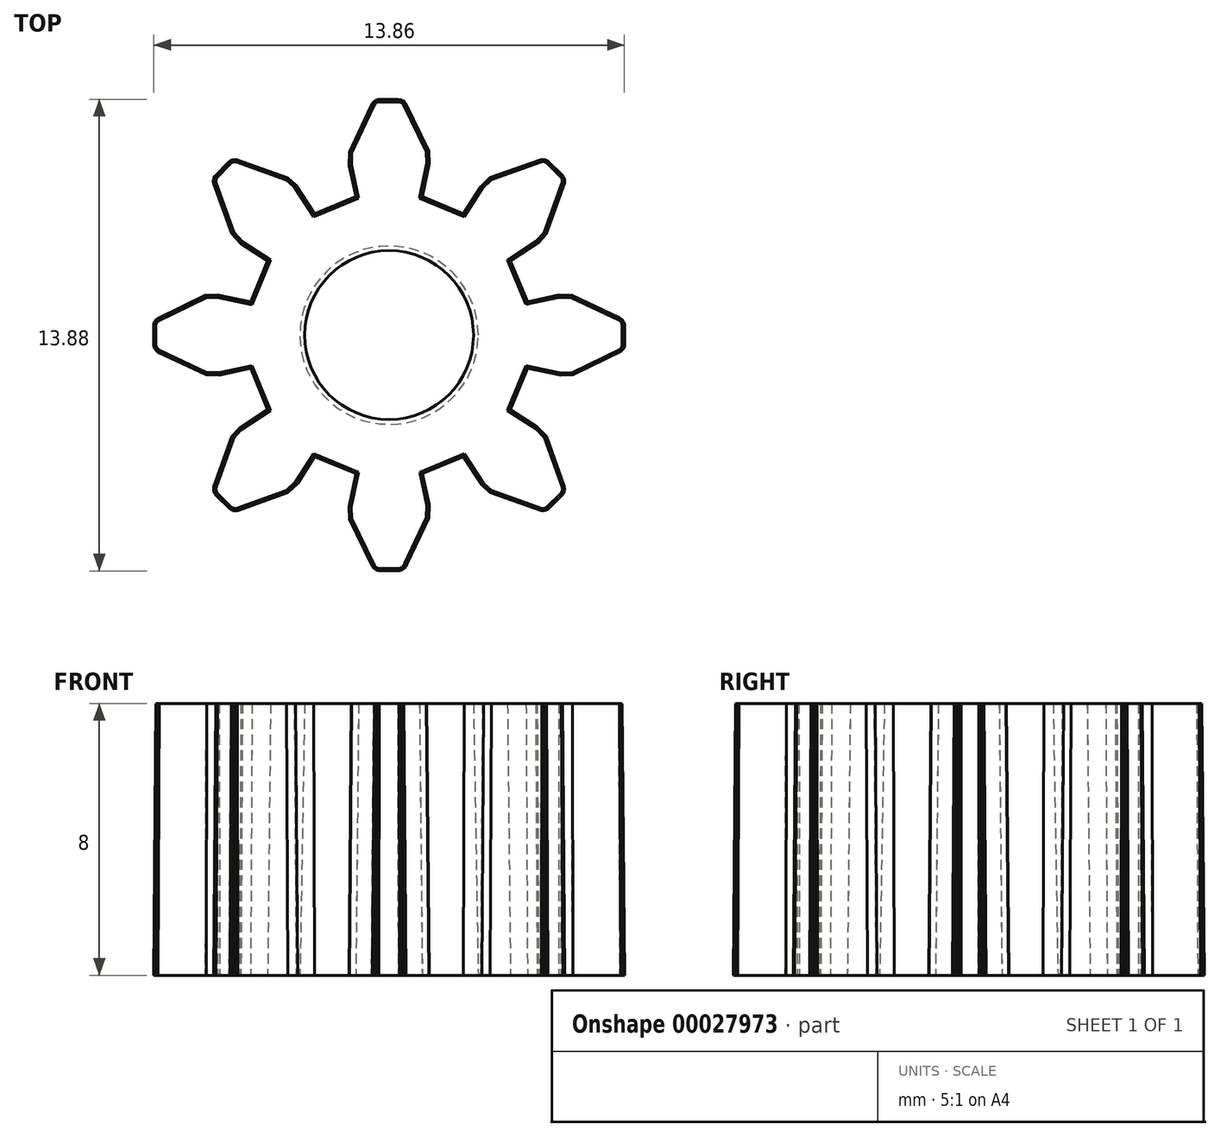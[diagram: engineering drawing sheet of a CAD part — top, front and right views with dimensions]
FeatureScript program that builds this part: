
annotation { "Feature Type Name" : "Feature", "Feature Type Description" : "" }
export const myFeature = defineFeature(function(context is Context, id is Id, definition is map)
    precondition{}
    {
        {
            var Q0;
            Q0=qCreatedBy(makeId("Top.planeOp"),FACE);
            var sketch = newSketch(context, id + "F0", { "sketchPlane" : qUnion([Q0])});
            skLineSegment(sketch, "E0", {"start": v(0.02, 6.93) * mm, "end": v(-0.31, 6.93) * mm});
            skLineSegment(sketch, "E1", {"start": v(-0.31, 6.93) * mm, "end": v(-0.39, 6.9) * mm});
            skLineSegment(sketch, "E2", {"start": v(-0.39, 6.9) * mm, "end": v(-0.43, 6.88) * mm});
            skLineSegment(sketch, "E3", {"start": v(-0.43, 6.88) * mm, "end": v(-0.48, 6.83) * mm});
            skLineSegment(sketch, "E4", {"start": v(-0.48, 6.83) * mm, "end": v(-0.53, 6.74) * mm});
            skLineSegment(sketch, "E5", {"start": v(-0.53, 6.74) * mm, "end": v(-1.17, 5.38) * mm});
            skLineSegment(sketch, "E6", {"start": v(-1.17, 5.38) * mm, "end": v(-1.18, 5) * mm});
            skLineSegment(sketch, "E7", {"start": v(-1.18, 5) * mm, "end": v(-0.98, 4.08) * mm});
            skLineSegment(sketch, "E8", {"start": v(-0.98, 4.08) * mm, "end": v(-2.2, 3.57) * mm});
            skLineSegment(sketch, "E9", {"start": v(-2.2, 3.57) * mm, "end": v(-2.74, 4.4) * mm});
            skLineSegment(sketch, "E10", {"start": v(-2.74, 4.4) * mm, "end": v(-2.98, 4.63) * mm});
            skLineSegment(sketch, "E11", {"start": v(-2.98, 4.63) * mm, "end": v(-4.48, 5.16) * mm});
            skLineSegment(sketch, "E12", {"start": v(-4.48, 5.16) * mm, "end": v(-4.52, 5.17) * mm});
            skLineSegment(sketch, "E13", {"start": v(-4.52, 5.17) * mm, "end": v(-4.6, 5.16) * mm});
            skLineSegment(sketch, "E14", {"start": v(-4.6, 5.16) * mm, "end": v(-4.65, 5.14) * mm});
            skLineSegment(sketch, "E15", {"start": v(-4.65, 5.14) * mm, "end": v(-4.72, 5.1) * mm});
            skLineSegment(sketch, "E16", {"start": v(-4.72, 5.1) * mm, "end": v(-5.12, 4.68) * mm});
            skLineSegment(sketch, "E17", {"start": v(-5.12, 4.68) * mm, "end": v(-5.16, 4.61) * mm});
            skLineSegment(sketch, "E18", {"start": v(-5.16, 4.61) * mm, "end": v(-5.17, 4.53) * mm});
            skLineSegment(sketch, "E19", {"start": v(-5.17, 4.53) * mm, "end": v(-5.16, 4.46) * mm});
            skLineSegment(sketch, "E20", {"start": v(-5.16, 4.46) * mm, "end": v(-4.63, 2.98) * mm});
            skLineSegment(sketch, "E21", {"start": v(-4.63, 2.98) * mm, "end": v(-4.36, 2.7) * mm});
            skLineSegment(sketch, "E22", {"start": v(-4.36, 2.7) * mm, "end": v(-3.57, 2.19) * mm});
            skLineSegment(sketch, "E23", {"start": v(-3.57, 2.19) * mm, "end": v(-4.08, 0.98) * mm});
            skLineSegment(sketch, "E24", {"start": v(-4.08, 0.98) * mm, "end": v(-5.05, 1.18) * mm});
            skLineSegment(sketch, "E25", {"start": v(-5.05, 1.18) * mm, "end": v(-5.42, 1.17) * mm});
            skLineSegment(sketch, "E26", {"start": v(-5.42, 1.17) * mm, "end": v(-6.82, 0.48) * mm});
            skLineSegment(sketch, "E27", {"start": v(-6.82, 0.48) * mm, "end": v(-6.86, 0.46) * mm});
            skLineSegment(sketch, "E28", {"start": v(-6.86, 0.46) * mm, "end": v(-6.9, 0.4) * mm});
            skLineSegment(sketch, "E29", {"start": v(-6.9, 0.4) * mm, "end": v(-6.93, 0.32) * mm});
            skLineSegment(sketch, "E30", {"start": v(-6.93, 0.32) * mm, "end": v(-6.93, 0.27) * mm});
            skLineSegment(sketch, "E31", {"start": v(-6.93, 0.27) * mm, "end": v(-6.93, -0.3) * mm});
            skLineSegment(sketch, "E32", {"start": v(-6.93, -0.3) * mm, "end": v(-6.9, -0.4) * mm});
            skLineSegment(sketch, "E33", {"start": v(-6.9, -0.4) * mm, "end": v(-6.86, -0.46) * mm});
            skLineSegment(sketch, "E34", {"start": v(-6.86, -0.46) * mm, "end": v(-6.8, -0.5) * mm});
            skLineSegment(sketch, "E35", {"start": v(-6.8, -0.5) * mm, "end": v(-5.38, -1.17) * mm});
            skLineSegment(sketch, "E36", {"start": v(-5.38, -1.17) * mm, "end": v(-5, -1.18) * mm});
            skLineSegment(sketch, "E37", {"start": v(-5, -1.18) * mm, "end": v(-4.08, -0.98) * mm});
            skLineSegment(sketch, "E38", {"start": v(-4.08, -0.98) * mm, "end": v(-3.57, -2.19) * mm});
            skLineSegment(sketch, "E39", {"start": v(-3.57, -2.19) * mm, "end": v(-4.4, -2.74) * mm});
            skLineSegment(sketch, "E40", {"start": v(-4.4, -2.74) * mm, "end": v(-4.63, -2.98) * mm});
            skLineSegment(sketch, "E41", {"start": v(-4.63, -2.98) * mm, "end": v(-5.16, -4.47) * mm});
            skLineSegment(sketch, "E42", {"start": v(-5.16, -4.47) * mm, "end": v(-5.17, -4.51) * mm});
            skLineSegment(sketch, "E43", {"start": v(-5.17, -4.51) * mm, "end": v(-5.16, -4.6) * mm});
            skLineSegment(sketch, "E44", {"start": v(-5.16, -4.6) * mm, "end": v(-5.13, -4.67) * mm});
            skLineSegment(sketch, "E45", {"start": v(-5.13, -4.67) * mm, "end": v(-5.1, -4.7) * mm});
            skLineSegment(sketch, "E46", {"start": v(-5.1, -4.7) * mm, "end": v(-4.68, -5.12) * mm});
            skLineSegment(sketch, "E47", {"start": v(-4.68, -5.12) * mm, "end": v(-4.6, -5.16) * mm});
            skLineSegment(sketch, "E48", {"start": v(-4.6, -5.16) * mm, "end": v(-4.53, -5.17) * mm});
            skLineSegment(sketch, "E49", {"start": v(-4.53, -5.17) * mm, "end": v(-4.46, -5.16) * mm});
            skLineSegment(sketch, "E50", {"start": v(-4.46, -5.16) * mm, "end": v(-2.98, -4.63) * mm});
            skLineSegment(sketch, "E51", {"start": v(-2.98, -4.63) * mm, "end": v(-2.7, -4.36) * mm});
            skLineSegment(sketch, "E52", {"start": v(-2.7, -4.36) * mm, "end": v(-2.2, -3.58) * mm});
            skLineSegment(sketch, "E53", {"start": v(-2.2, -3.58) * mm, "end": v(-0.98, -4.08) * mm});
            skLineSegment(sketch, "E54", {"start": v(-0.98, -4.08) * mm, "end": v(-1.18, -5.05) * mm});
            skLineSegment(sketch, "E55", {"start": v(-1.18, -5.05) * mm, "end": v(-1.17, -5.42) * mm});
            skLineSegment(sketch, "E56", {"start": v(-1.17, -5.42) * mm, "end": v(-0.5, -6.81) * mm});
            skLineSegment(sketch, "E57", {"start": v(-0.5, -6.81) * mm, "end": v(-0.47, -6.85) * mm});
            skLineSegment(sketch, "E58", {"start": v(-0.47, -6.85) * mm, "end": v(-0.4, -6.9) * mm});
            skLineSegment(sketch, "E59", {"start": v(-0.4, -6.9) * mm, "end": v(-0.37, -6.92) * mm});
            skLineSegment(sketch, "E60", {"start": v(-0.37, -6.92) * mm, "end": v(-0.3, -6.93) * mm});
            skLineSegment(sketch, "E61", {"start": v(-0.3, -6.93) * mm, "end": v(0.3, -6.93) * mm});
            skLineSegment(sketch, "E62", {"start": v(0.3, -6.93) * mm, "end": v(0.39, -6.9) * mm});
            skLineSegment(sketch, "E63", {"start": v(0.39, -6.9) * mm, "end": v(0.46, -6.86) * mm});
            skLineSegment(sketch, "E64", {"start": v(0.46, -6.86) * mm, "end": v(0.5, -6.8) * mm});
            skLineSegment(sketch, "E65", {"start": v(0.5, -6.8) * mm, "end": v(0.53, -6.74) * mm});
            skLineSegment(sketch, "E66", {"start": v(0.53, -6.74) * mm, "end": v(1.17, -5.38) * mm});
            skLineSegment(sketch, "E67", {"start": v(1.17, -5.38) * mm, "end": v(1.18, -5) * mm});
            skLineSegment(sketch, "E68", {"start": v(1.18, -5) * mm, "end": v(0.98, -4.08) * mm});
            skLineSegment(sketch, "E69", {"start": v(0.98, -4.08) * mm, "end": v(2.19, -3.58) * mm});
            skLineSegment(sketch, "E70", {"start": v(2.19, -3.58) * mm, "end": v(2.74, -4.4) * mm});
            skLineSegment(sketch, "E71", {"start": v(2.74, -4.4) * mm, "end": v(2.98, -4.63) * mm});
            skLineSegment(sketch, "E72", {"start": v(2.98, -4.63) * mm, "end": v(4.48, -5.17) * mm});
            skLineSegment(sketch, "E73", {"start": v(4.48, -5.17) * mm, "end": v(4.57, -5.17) * mm});
            skLineSegment(sketch, "E74", {"start": v(4.57, -5.17) * mm, "end": v(4.61, -5.16) * mm});
            skLineSegment(sketch, "E75", {"start": v(4.61, -5.16) * mm, "end": v(4.68, -5.12) * mm});
            skLineSegment(sketch, "E76", {"start": v(4.68, -5.12) * mm, "end": v(5.12, -4.68) * mm});
            skLineSegment(sketch, "E77", {"start": v(5.12, -4.68) * mm, "end": v(5.16, -4.6) * mm});
            skLineSegment(sketch, "E78", {"start": v(5.16, -4.6) * mm, "end": v(5.17, -4.53) * mm});
            skLineSegment(sketch, "E79", {"start": v(5.17, -4.53) * mm, "end": v(5.16, -4.46) * mm});
            skLineSegment(sketch, "E80", {"start": v(5.16, -4.46) * mm, "end": v(4.63, -2.98) * mm});
            skLineSegment(sketch, "E81", {"start": v(4.63, -2.98) * mm, "end": v(4.36, -2.7) * mm});
            skLineSegment(sketch, "E82", {"start": v(4.36, -2.7) * mm, "end": v(3.57, -2.19) * mm});
            skLineSegment(sketch, "E83", {"start": v(3.57, -2.19) * mm, "end": v(4.08, -0.98) * mm});
            skLineSegment(sketch, "E84", {"start": v(4.08, -0.98) * mm, "end": v(5.05, -1.18) * mm});
            skLineSegment(sketch, "E85", {"start": v(5.05, -1.18) * mm, "end": v(5.42, -1.17) * mm});
            skLineSegment(sketch, "E86", {"start": v(5.42, -1.17) * mm, "end": v(6.82, -0.48) * mm});
            skLineSegment(sketch, "E87", {"start": v(6.82, -0.48) * mm, "end": v(6.88, -0.43) * mm});
            skLineSegment(sketch, "E88", {"start": v(6.88, -0.43) * mm, "end": v(6.9, -0.39) * mm});
            skLineSegment(sketch, "E89", {"start": v(6.9, -0.39) * mm, "end": v(6.93, -0.32) * mm});
            skLineSegment(sketch, "E90", {"start": v(6.93, -0.32) * mm, "end": v(6.93, -0.23) * mm});
            skLineSegment(sketch, "E91", {"start": v(6.93, -0.23) * mm, "end": v(6.93, 0.3) * mm});
            skLineSegment(sketch, "E92", {"start": v(6.93, 0.3) * mm, "end": v(6.9, 0.39) * mm});
            skLineSegment(sketch, "E93", {"start": v(6.9, 0.39) * mm, "end": v(6.86, 0.46) * mm});
            skLineSegment(sketch, "E94", {"start": v(6.86, 0.46) * mm, "end": v(6.8, 0.5) * mm});
            skLineSegment(sketch, "E95", {"start": v(6.8, 0.5) * mm, "end": v(5.38, 1.17) * mm});
            skLineSegment(sketch, "E96", {"start": v(5.38, 1.17) * mm, "end": v(5, 1.18) * mm});
            skLineSegment(sketch, "E97", {"start": v(5, 1.18) * mm, "end": v(4.08, 0.98) * mm});
            skLineSegment(sketch, "E98", {"start": v(4.08, 0.98) * mm, "end": v(3.57, 2.19) * mm});
            skLineSegment(sketch, "E99", {"start": v(3.57, 2.19) * mm, "end": v(4.4, 2.74) * mm});
            skLineSegment(sketch, "E100", {"start": v(4.4, 2.74) * mm, "end": v(4.63, 2.98) * mm});
            skLineSegment(sketch, "E101", {"start": v(4.63, 2.98) * mm, "end": v(5.17, 4.48) * mm});
            skLineSegment(sketch, "E102", {"start": v(5.17, 4.48) * mm, "end": v(5.17, 4.54) * mm});
            skLineSegment(sketch, "E103", {"start": v(5.17, 4.54) * mm, "end": v(5.16, 4.6) * mm});
            skLineSegment(sketch, "E104", {"start": v(5.16, 4.6) * mm, "end": v(5.13, 4.67) * mm});
            skLineSegment(sketch, "E105", {"start": v(5.13, 4.67) * mm, "end": v(5.1, 4.7) * mm});
            skLineSegment(sketch, "E106", {"start": v(5.1, 4.7) * mm, "end": v(4.68, 5.12) * mm});
            skLineSegment(sketch, "E107", {"start": v(4.68, 5.12) * mm, "end": v(4.6, 5.16) * mm});
            skLineSegment(sketch, "E108", {"start": v(4.6, 5.16) * mm, "end": v(4.53, 5.17) * mm});
            skLineSegment(sketch, "E109", {"start": v(4.53, 5.17) * mm, "end": v(4.46, 5.16) * mm});
            skLineSegment(sketch, "E110", {"start": v(4.46, 5.16) * mm, "end": v(2.98, 4.63) * mm});
            skLineSegment(sketch, "E111", {"start": v(2.98, 4.63) * mm, "end": v(2.7, 4.36) * mm});
            skLineSegment(sketch, "E112", {"start": v(2.7, 4.36) * mm, "end": v(2.19, 3.57) * mm});
            skLineSegment(sketch, "E113", {"start": v(2.19, 3.57) * mm, "end": v(0.98, 4.08) * mm});
            skLineSegment(sketch, "E114", {"start": v(0.98, 4.08) * mm, "end": v(1.18, 5.05) * mm});
            skLineSegment(sketch, "E115", {"start": v(1.18, 5.05) * mm, "end": v(1.17, 5.42) * mm});
            skLineSegment(sketch, "E116", {"start": v(1.17, 5.42) * mm, "end": v(0.49, 6.82) * mm});
            skLineSegment(sketch, "E117", {"start": v(0.49, 6.82) * mm, "end": v(0.43, 6.88) * mm});
            skLineSegment(sketch, "E118", {"start": v(0.43, 6.88) * mm, "end": v(0.35, 6.92) * mm});
            skLineSegment(sketch, "E119", {"start": v(0.35, 6.92) * mm, "end": v(0.26, 6.93) * mm});
            skLineSegment(sketch, "E120", {"start": v(0.26, 6.93) * mm, "end": v(0.02, 6.93) * mm});
            skSolve(sketch);
        }
        {
            var Q0;
            Q0=qCreatedBy(makeId("Top.planeOp"),FACE);
            var sketch = newSketch(context, id + "F1", { "sketchPlane" : qUnion([Q0])});
            skCircle(sketch, "E121", {"center": v(0, 0) * mm, "radius": 2.62 * mm});
            skSolve(sketch);
        }
        {
            var Q0;
            Q0 = qSketchRegion(id + "F0", true);
            extrude(context, id + "F2", {"entities" : qUnion([Q0]), "depth" : 8 * mm, "hasDraft" : true, "draftAngle" : .5 * degree, "draftPullDirection" : true});
        }
        {
            var Q0;
            Q0 = qSketchRegion(id + "F1", true);
            var Q1;
            Q1=makeQuery(id+"F2.opExtrude","CAP_FACE",FACE,{"disambiguationData":[OSD([sQuery(id+"F0.wireOp",EDGE,"E0"),sQuery(id+"F0.wireOp",EDGE,"E1"),sQuery(id+"F0.wireOp",EDGE,"E2"),sQuery(id+"F0.wireOp",EDGE,"E3"),sQuery(id+"F0.wireOp",EDGE,"E4"),sQuery(id+"F0.wireOp",EDGE,"E5"),sQuery(id+"F0.wireOp",EDGE,"E6"),sQuery(id+"F0.wireOp",EDGE,"E7"),sQuery(id+"F0.wireOp",EDGE,"E8"),sQuery(id+"F0.wireOp",EDGE,"E9"),sQuery(id+"F0.wireOp",EDGE,"E10"),sQuery(id+"F0.wireOp",EDGE,"E11"),sQuery(id+"F0.wireOp",EDGE,"E12"),sQuery(id+"F0.wireOp",EDGE,"E13"),sQuery(id+"F0.wireOp",EDGE,"E14"),sQuery(id+"F0.wireOp",EDGE,"E15"),sQuery(id+"F0.wireOp",EDGE,"E16"),sQuery(id+"F0.wireOp",EDGE,"E17"),sQuery(id+"F0.wireOp",EDGE,"E18"),sQuery(id+"F0.wireOp",EDGE,"E19"),sQuery(id+"F0.wireOp",EDGE,"E20"),sQuery(id+"F0.wireOp",EDGE,"E21"),sQuery(id+"F0.wireOp",EDGE,"E22"),sQuery(id+"F0.wireOp",EDGE,"E23"),sQuery(id+"F0.wireOp",EDGE,"E24"),sQuery(id+"F0.wireOp",EDGE,"E25"),sQuery(id+"F0.wireOp",EDGE,"E26"),sQuery(id+"F0.wireOp",EDGE,"E27"),sQuery(id+"F0.wireOp",EDGE,"E28"),sQuery(id+"F0.wireOp",EDGE,"E29"),sQuery(id+"F0.wireOp",EDGE,"E30"),sQuery(id+"F0.wireOp",EDGE,"E31"),sQuery(id+"F0.wireOp",EDGE,"E32"),sQuery(id+"F0.wireOp",EDGE,"E33"),sQuery(id+"F0.wireOp",EDGE,"E34"),sQuery(id+"F0.wireOp",EDGE,"E35"),sQuery(id+"F0.wireOp",EDGE,"E36"),sQuery(id+"F0.wireOp",EDGE,"E37"),sQuery(id+"F0.wireOp",EDGE,"E38"),sQuery(id+"F0.wireOp",EDGE,"E39"),sQuery(id+"F0.wireOp",EDGE,"E40"),sQuery(id+"F0.wireOp",EDGE,"E41"),sQuery(id+"F0.wireOp",EDGE,"E42"),sQuery(id+"F0.wireOp",EDGE,"E43"),sQuery(id+"F0.wireOp",EDGE,"E44"),sQuery(id+"F0.wireOp",EDGE,"E45"),sQuery(id+"F0.wireOp",EDGE,"E46"),sQuery(id+"F0.wireOp",EDGE,"E47"),sQuery(id+"F0.wireOp",EDGE,"E48"),sQuery(id+"F0.wireOp",EDGE,"E49"),sQuery(id+"F0.wireOp",EDGE,"E50"),sQuery(id+"F0.wireOp",EDGE,"E51"),sQuery(id+"F0.wireOp",EDGE,"E52"),sQuery(id+"F0.wireOp",EDGE,"E53"),sQuery(id+"F0.wireOp",EDGE,"E54"),sQuery(id+"F0.wireOp",EDGE,"E55"),sQuery(id+"F0.wireOp",EDGE,"E56"),sQuery(id+"F0.wireOp",EDGE,"E57"),sQuery(id+"F0.wireOp",EDGE,"E58"),sQuery(id+"F0.wireOp",EDGE,"E59"),sQuery(id+"F0.wireOp",EDGE,"E60"),sQuery(id+"F0.wireOp",EDGE,"E61"),sQuery(id+"F0.wireOp",EDGE,"E62"),sQuery(id+"F0.wireOp",EDGE,"E63"),sQuery(id+"F0.wireOp",EDGE,"E64"),sQuery(id+"F0.wireOp",EDGE,"E65"),sQuery(id+"F0.wireOp",EDGE,"E66"),sQuery(id+"F0.wireOp",EDGE,"E67"),sQuery(id+"F0.wireOp",EDGE,"E68"),sQuery(id+"F0.wireOp",EDGE,"E69"),sQuery(id+"F0.wireOp",EDGE,"E70"),sQuery(id+"F0.wireOp",EDGE,"E71"),sQuery(id+"F0.wireOp",EDGE,"E72"),sQuery(id+"F0.wireOp",EDGE,"E73"),sQuery(id+"F0.wireOp",EDGE,"E74"),sQuery(id+"F0.wireOp",EDGE,"E75"),sQuery(id+"F0.wireOp",EDGE,"E76"),sQuery(id+"F0.wireOp",EDGE,"E77"),sQuery(id+"F0.wireOp",EDGE,"E78"),sQuery(id+"F0.wireOp",EDGE,"E79"),sQuery(id+"F0.wireOp",EDGE,"E80"),sQuery(id+"F0.wireOp",EDGE,"E81"),sQuery(id+"F0.wireOp",EDGE,"E82"),sQuery(id+"F0.wireOp",EDGE,"E83"),sQuery(id+"F0.wireOp",EDGE,"E84"),sQuery(id+"F0.wireOp",EDGE,"E85"),sQuery(id+"F0.wireOp",EDGE,"E86"),sQuery(id+"F0.wireOp",EDGE,"E87"),sQuery(id+"F0.wireOp",EDGE,"E88"),sQuery(id+"F0.wireOp",EDGE,"E89"),sQuery(id+"F0.wireOp",EDGE,"E90"),sQuery(id+"F0.wireOp",EDGE,"E91"),sQuery(id+"F0.wireOp",EDGE,"E92"),sQuery(id+"F0.wireOp",EDGE,"E93"),sQuery(id+"F0.wireOp",EDGE,"E94"),sQuery(id+"F0.wireOp",EDGE,"E95"),sQuery(id+"F0.wireOp",EDGE,"E96"),sQuery(id+"F0.wireOp",EDGE,"E97"),sQuery(id+"F0.wireOp",EDGE,"E98"),sQuery(id+"F0.wireOp",EDGE,"E99"),sQuery(id+"F0.wireOp",EDGE,"E100"),sQuery(id+"F0.wireOp",EDGE,"E101"),sQuery(id+"F0.wireOp",EDGE,"E102"),sQuery(id+"F0.wireOp",EDGE,"E103"),sQuery(id+"F0.wireOp",EDGE,"E104"),sQuery(id+"F0.wireOp",EDGE,"E105"),sQuery(id+"F0.wireOp",EDGE,"E106"),sQuery(id+"F0.wireOp",EDGE,"E107"),sQuery(id+"F0.wireOp",EDGE,"E108"),sQuery(id+"F0.wireOp",EDGE,"E109"),sQuery(id+"F0.wireOp",EDGE,"E110"),sQuery(id+"F0.wireOp",EDGE,"E111"),sQuery(id+"F0.wireOp",EDGE,"E112"),sQuery(id+"F0.wireOp",EDGE,"E113"),sQuery(id+"F0.wireOp",EDGE,"E114"),sQuery(id+"F0.wireOp",EDGE,"E115"),sQuery(id+"F0.wireOp",EDGE,"E116"),sQuery(id+"F0.wireOp",EDGE,"E117"),sQuery(id+"F0.wireOp",EDGE,"E118"),sQuery(id+"F0.wireOp",EDGE,"E119"),sQuery(id+"F0.wireOp",EDGE,"E120")])],"isStart":false});
            extrude(context, id + "F3", {"entities" : qUnion([Q0]), "operationType" : NewBodyOperationType.REMOVE, "endBound" : BoundingType.UP_TO_SURFACE, "endBoundEntityFace" : qUnion([Q1]), "depth" : 8 * mm, "hasDraft" : true, "draftAngle" : 1 * degree, "draftPullDirection" : true});
        }
    });
